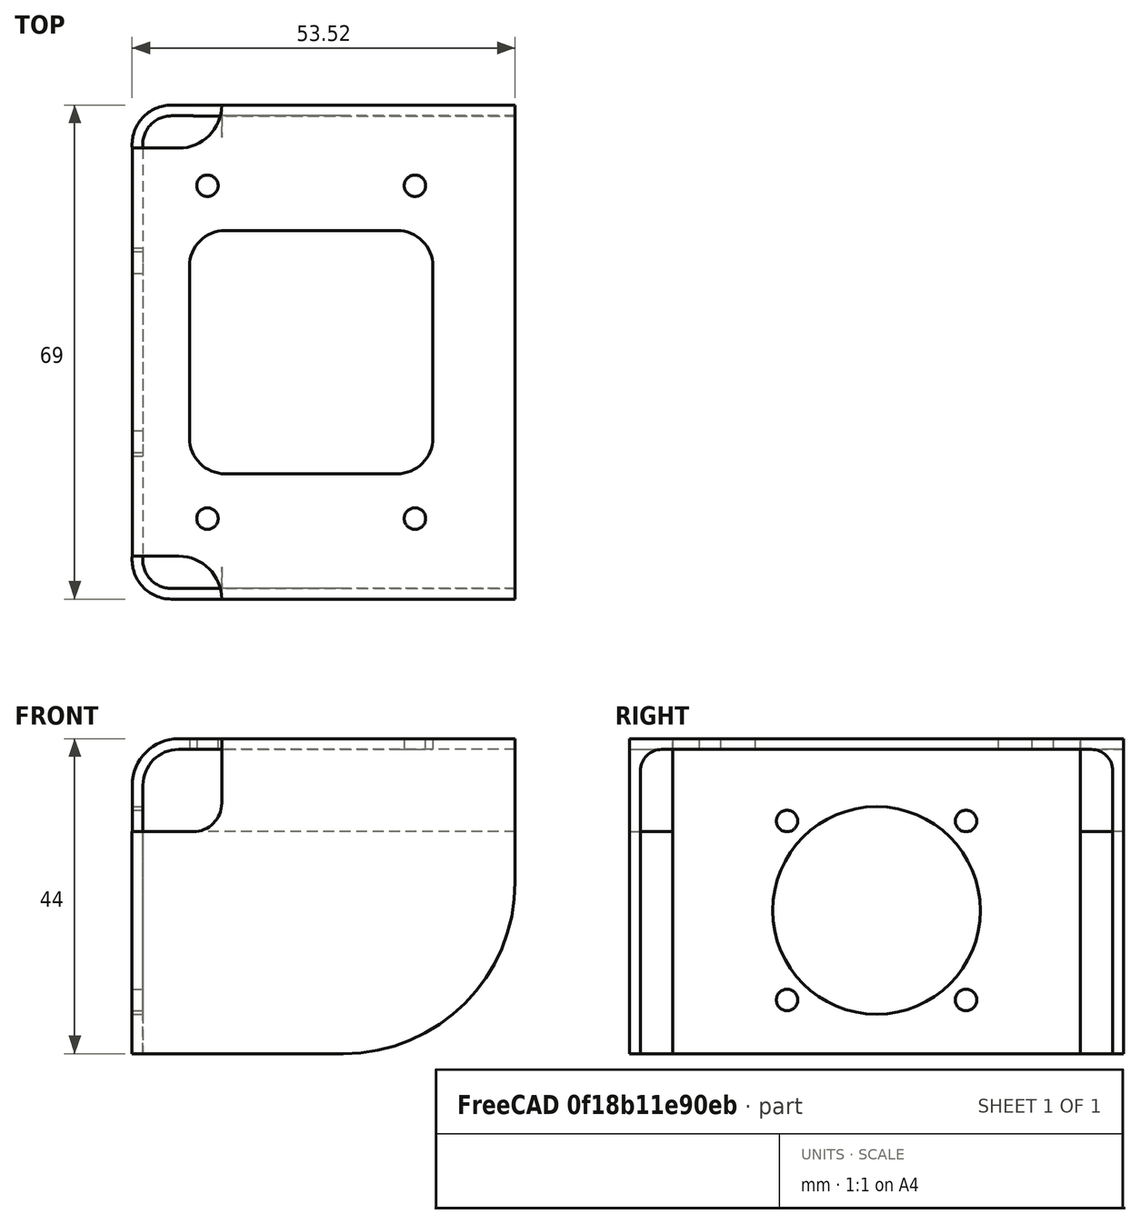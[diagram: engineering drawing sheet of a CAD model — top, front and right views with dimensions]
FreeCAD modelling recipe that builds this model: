
FCSTD DOCUMENT  (FreeCAD 0.19R)
Label: tole_adaptation_extrudeur_tete_mobile
License: All rights reserved
LicenseURL: http://en.wikipedia.org/wiki/All_rights_reserved
objects: TechDraw::DrawViewDimension×19, Sketcher::SketchObject×5, TechDraw::DrawViewPart×4, PartDesign::Pad×3, PartDesign::Pocket×2, PartDesign::Fillet×2, PartDesign::Mirrored×1, PartDesign::Body×1, TechDraw::DrawSVGTemplate×1, TechDraw::DrawPage×1
note: 21 computed .brp shape members not serialized (recipe doc carries the construction recipe); baked Part::Feature solids carry a one-line shape summary decoded from their .brp

FEATURE [Sketcher::SketchObject] Sketch
  FullyConstrained = true
  MapMode = 5
  Placement = pos=(0,0,0) rot=(1,0,0;1.5708rad)
  Support = -> [XZ_Plane]
  sketch-geometry (8):
    g0: LineSegment StartX=0 StartY=-44 StartZ=0 EndX=0 EndY=-6.5 EndZ=0
    g1: LineSegment StartX=6.5 StartY=0 StartZ=0 EndX=53.5 EndY=0 EndZ=0
    g2: LineSegment StartX=53.5 StartY=0 StartZ=0 EndX=53.5 EndY=-1.5 EndZ=0
    g3: LineSegment StartX=53.5 StartY=-1.5 StartZ=0 EndX=6.5 EndY=-1.5 EndZ=0
    g4: LineSegment StartX=1.5 StartY=-6.5 StartZ=0 EndX=1.5 EndY=-44 EndZ=0
    g5: LineSegment StartX=1.5 StartY=-44 StartZ=0 EndX=0 EndY=-44 EndZ=0
    g6: ArcOfCircle CenterX=6.5 CenterY=-6.5 CenterZ=0 NormalX=0 NormalY=0 NormalZ=1 AngleXU=0 Radius=5 StartAngle=1.5708 EndAngle=3.14159
    g7: ArcOfCircle CenterX=6.5 CenterY=-6.5 CenterZ=0 NormalX=0 NormalY=0 NormalZ=1 AngleXU=0 Radius=6.5 StartAngle=1.5708 EndAngle=3.14159
  constraints (21):
    c: PointOnObject(g0,g-2)
    c: PointOnObject(g1,g-1)
    c: Coincident(g1,g2)
    c: Vertical(g2)
    c: Coincident(g2,g3)
    c: Horizontal(g3)
    c: Vertical(g4)
    c: Coincident(g4,g5)
    c: Coincident(g5,g0)
    c: Tangent(g4,g6) = -1.5708
    c: Tangent(g3,g6) = -1.5708
    c: Tangent(g0,g7) = 1.5708
    c: Tangent(g1,g7) = 1.5708
    c: Coincident(g7,g6)
    c: Vertical(g0)
    c: Horizontal(g1)
    c: Horizontal(g5)
    c: DistanceY(g2,g2) = 1.5
    c: Radius(g6) = 5
    c: DistanceX(g-1,g1) = 53.5
    c: DistanceY(g0,g-1) = 44
FEATURE [PartDesign::Pad] Pad
  Direction = (1,1,1)
  Length = 69
  Length2 = 100
  Midplane = true
  Placement = pos=(0,0,0) rot=(1,0,0;1.5708rad)
  Profile = -> Sketch
  Type = 0
FEATURE [Sketcher::SketchObject] Sketch001
  ExternalGeometry = -> [Pad]
  FullyConstrained = false
  MapMode = 5
  Placement = pos=(0,0,0) rot=(0,0,1;3.14159rad)
  Support = -> [Pad]
  sketch-geometry (21):
    g0: LineSegment StartX=-37 StartY=17 StartZ=0 EndX=-13 EndY=17 EndZ=0
    g1: LineSegment StartX=-8 StartY=12 StartZ=0 EndX=-8 EndY=-12 EndZ=0
    g2: LineSegment StartX=-13 StartY=-17 StartZ=0 EndX=-37 EndY=-17 EndZ=0
    g3: LineSegment StartX=-42 StartY=-12 StartZ=0 EndX=-42 EndY=12 EndZ=0
    g4: ArcOfCircle CenterX=-13 CenterY=12 CenterZ=0 NormalX=0 NormalY=0 NormalZ=1 AngleXU=0 Radius=5 StartAngle=0 EndAngle=1.5708
    g5: ArcOfCircle CenterX=-37 CenterY=12 CenterZ=0 NormalX=0 NormalY=0 NormalZ=1 AngleXU=0 Radius=5 StartAngle=1.5708 EndAngle=3.14159
    g6: ArcOfCircle CenterX=-37 CenterY=-12 CenterZ=0 NormalX=0 NormalY=0 NormalZ=1 AngleXU=0 Radius=5 StartAngle=3.14159 EndAngle=4.71239
    g7: ArcOfCircle CenterX=-13 CenterY=-12 CenterZ=0 NormalX=0 NormalY=0 NormalZ=1 AngleXU=0 Radius=5 StartAngle=4.71239 EndAngle=6.28319
    g8: LineSegment StartX=-25 StartY=36.475 StartZ=0 EndX=-25 EndY=-28.4606 EndZ=0
    g9: Circle CenterX=-39.5 CenterY=23.25 CenterZ=0 NormalX=0 NormalY=0 NormalZ=1 AngleXU=0 Radius=1.5
    g10: Circle CenterX=-10.5 CenterY=23.25 CenterZ=0 NormalX=0 NormalY=0 NormalZ=1 AngleXU=0 Radius=1.5
    g11: Circle CenterX=-10.5 CenterY=-23.25 CenterZ=0 NormalX=0 NormalY=0 NormalZ=1 AngleXU=0 Radius=1.5
    g12: Circle CenterX=-39.5 CenterY=-23.25 CenterZ=0 NormalX=0 NormalY=0 NormalZ=1 AngleXU=0 Radius=1.5
    g13: ArcOfCircle CenterX=-6.5 CenterY=34.5 CenterZ=0 NormalX=0 NormalY=0 NormalZ=1 AngleXU=0 Radius=6 StartAngle=3.14159 EndAngle=4.71239
    g14: LineSegment StartX=-6.5 StartY=28.5 StartZ=0 EndX=1 EndY=28.5 EndZ=0
    g15: LineSegment StartX=-12.5 StartY=34.5 StartZ=0 EndX=1 EndY=34.5 EndZ=0
    g16: LineSegment StartX=1 StartY=34.5 StartZ=0 EndX=1 EndY=28.5 EndZ=0
    g17: ArcOfCircle CenterX=-6.5 CenterY=-34.5 CenterZ=0 NormalX=0 NormalY=0 NormalZ=1 AngleXU=0 Radius=6 StartAngle=1.5708 EndAngle=3.14159
    g18: LineSegment StartX=-6.5 StartY=-28.5 StartZ=0 EndX=1 EndY=-28.5 EndZ=0
    g19: LineSegment StartX=1 StartY=-28.5 StartZ=0 EndX=1 EndY=-34.5 EndZ=0
    g20: LineSegment StartX=1 StartY=-34.5 StartZ=0 EndX=-12.5 EndY=-34.5 EndZ=0
  constraints (49):
    c: Horizontal(g0)
    c: Tangent(g0,g4) = 1.5708
    c: Tangent(g1,g4) = 1.5708
    c: Tangent(g3,g5) = 1.5708
    c: Tangent(g0,g5) = 1.5708
    c: Tangent(g2,g6) = 1.5708
    c: Tangent(g3,g6) = 1.5708
    c: Tangent(g2,g7) = 1.5708
    c: Tangent(g1,g7) = 1.5708
    c: Symmetric(g0,g0,g8)
    c: Symmetric(g3,g1,g8)
    c: Symmetric(g2,g2,g8)
    c: Symmetric(g3,g3,g-1)
    c: Radius(g4) = 5
    c: DistanceY(g2,g0) = 34
    c: DistanceX(g3,g1) = 34
    c: Equal(g4,g7)
    c: DistanceX(g1,g-1) = 8
    c: DistanceX(g9,g10) = 29
    c: Symmetric(g9,g10,g8)
    c: Symmetric(g9,g12,g-1)
    c: Symmetric(g12,g11,g8)
    c: Equal(g11,g12)
    c: Equal(g11,g10)
    c: Equal(g9,g10)
    c: Radius(g9) = 1.5
    c: DistanceY(g12,g9) = 46.5
    c: Coincident(g13,g-3)
    c: PointOnObject(g13,g-3)
    c: Horizontal(g14)
    c: Tangent(g14,g13) = -1.5708
    c: Coincident(g15,g13)
    c: Horizontal(g15)
    c: Coincident(g16,g15)
    c: Coincident(g16,g14)
    c: Vertical(g16)
    c: DistanceX(g-1,g15) = 1
    c: Radius(g13) = 6
    c: Coincident(g17,g-4)
    c: PointOnObject(g17,g-4)
    c: Tangent(g17,g18) = 1.5708
    c: Coincident(g18,g19)
    c: Vertical(g19)
    c: Coincident(g19,g20)
    c: Coincident(g20,g17)
    c: Horizontal(g20)
    c: DistanceX(g-1,g18) = 1
    c: Horizontal(g18)
    c: Equal(g17,g13)
FEATURE [PartDesign::Pocket] Pocket
  BaseFeature = -> Pad
  Length = 5
  Length2 = 100
  Placement = pos=(0,0,0) rot=(1,0,0;1.5708rad)
  Profile = -> Sketch001
  Type = 1
FEATURE [Sketcher::SketchObject] Sketch003
  FullyConstrained = true
  MapMode = 5
  Placement = pos=(0,0,0) rot=(0.57735,0.57735,0.57735;2.0944rad)
  Support = -> [YZ_Plane]
  sketch-geometry (10):
    g0: Circle CenterX=0 CenterY=-24 CenterZ=0 NormalX=0 NormalY=0 NormalZ=1 AngleXU=0 Radius=14.5
    g1: LineSegment StartX=-12.5 StartY=-11.5 StartZ=0 EndX=12.5 EndY=-11.5 EndZ=0
    g2: LineSegment StartX=12.5 StartY=-11.5 StartZ=0 EndX=12.5 EndY=-36.5 EndZ=0
    g3: LineSegment StartX=12.5 StartY=-36.5 StartZ=0 EndX=-12.5 EndY=-36.5 EndZ=0
    g4: LineSegment StartX=-12.5 StartY=-36.5 StartZ=0 EndX=-12.5 EndY=-11.5 EndZ=0
    g5: Circle CenterX=12.5 CenterY=-11.5 CenterZ=0 NormalX=0 NormalY=0 NormalZ=1 AngleXU=0 Radius=1.5
    g6: Circle CenterX=-12.5 CenterY=-11.5 CenterZ=0 NormalX=0 NormalY=0 NormalZ=1 AngleXU=0 Radius=1.5
    g7: Circle CenterX=-12.5 CenterY=-36.5 CenterZ=0 NormalX=0 NormalY=0 NormalZ=1 AngleXU=0 Radius=1.5
    g8: Circle CenterX=12.5 CenterY=-36.5 CenterZ=0 NormalX=0 NormalY=0 NormalZ=1 AngleXU=0 Radius=1.5
    g9: LineSegment StartX=-12.5 StartY=-11.5 StartZ=0 EndX=12.5 EndY=-36.5 EndZ=0
  constraints (24):
    c: Radius(g0) = 14.5
    c: Coincident(g1,g2)
    c: Coincident(g2,g3)
    c: Coincident(g3,g4)
    c: Coincident(g4,g1)
    c: Horizontal(g3)
    c: Vertical(g2)
    c: Coincident(g5,g1)
    c: Coincident(g6,g1)
    c: Coincident(g7,g3)
    c: Coincident(g8,g2)
    c: Equal(g8,g5)
    c: Equal(g5,g6)
    c: Equal(g6,g7)
    c: Radius(g6) = 1.5
    c: DistanceY(g2,g2) = 25
    c: DistanceX(g1,g1) = 25
    c: Coincident(g9,g6)
    c: Coincident(g9,g8)
    c: PointOnObject(g0,g9)
    c: Vertical(g4)
    c: Symmetric(g5,g6,g-2)
    c: PointOnObject(g0,g-2)
    c: DistanceY(g0,g-1) = 24
FEATURE [PartDesign::Pocket] Pocket001
  BaseFeature = -> Pocket
  Length = 5
  Length2 = 100
  Midplane = true
  Placement = pos=(0,0,0) rot=(1,0,0;1.5708rad)
  Profile = -> Sketch003
  Type = 1
FEATURE [Sketcher::SketchObject] Sketch004
  ExternalGeometry = -> [Pocket001]
  FullyConstrained = true
  MapMode = 5
  Placement = pos=(0,-6.84e-14,-44) rot=(1,0,0;3.14159rad)
  Support = -> [Pocket001]
  sketch-geometry (6):
    g0: ArcOfCircle CenterX=5.4675 CenterY=29.0089 CenterZ=0 NormalX=0 NormalY=0 NormalZ=1 AngleXU=0 Radius=4 StartAngle=1.5708 EndAngle=3.26916
    g1: ArcOfCircle CenterX=5.4675 CenterY=29.0089 CenterZ=0 NormalX=0 NormalY=0 NormalZ=1 AngleXU=0 Radius=5.49113 StartAngle=1.5708 EndAngle=3.2344
    g2: LineSegment StartX=5.4675 StartY=34.5 StartZ=0 EndX=53.5 EndY=34.5 EndZ=0
    g3: LineSegment StartX=53.5 StartY=34.5 StartZ=0 EndX=53.5 EndY=33.0089 EndZ=0
    g4: LineSegment StartX=53.5 StartY=33.0089 StartZ=0 EndX=5.4675 EndY=33.0089 EndZ=0
    g5: LineSegment StartX=0 StartY=28.5 StartZ=0 EndX=1.5 EndY=28.5 EndZ=0
  constraints (14):
    c: Coincident(g1,g0)
    c: Tangent(g1,g2) = 1.5708
    c: Coincident(g2,g3)
    c: Vertical(g3)
    c: Coincident(g3,g4)
    c: Horizontal(g4)
    c: Horizontal(g2)
    c: Radius(g0) = 4
    c: Coincident(g5,g1)
    c: Coincident(g5,g0)
    c: Coincident(g-3,g0)
    c: Coincident(g1,g-4)
    c: Tangent(g4,g0) = -1.5708
    c: Coincident(g-5,g2)
FEATURE [PartDesign::Pad] Pad001
  BaseFeature = -> Pocket001
  Direction = (1,1,1)
  Length = 31
  Length2 = 100
  Placement = pos=(0,0,0) rot=(1,0,0;1.5708rad)
  Profile = -> Sketch004
  Reversed = true
  Type = 0
FEATURE [Sketcher::SketchObject] Sketch005
  ExternalGeometry = -> [Pad001]
  FullyConstrained = true
  MapMode = 5
  Placement = pos=(0,-34.5,6.89e-14) rot=(1,0,0;1.5708rad)
  Support = -> [Pad001]
  sketch-geometry (5):
    g0: LineSegment StartX=53.5 StartY=-1.5 StartZ=0 EndX=12.5 EndY=-1.5 EndZ=0
    g1: LineSegment StartX=12.5 StartY=-1.5 StartZ=0 EndX=12.5 EndY=-9 EndZ=0
    g2: LineSegment StartX=8.5 StartY=-13 StartZ=0 EndX=53.5 EndY=-13 EndZ=0
    g3: LineSegment StartX=53.5 StartY=-13 StartZ=0 EndX=53.5 EndY=-1.5 EndZ=0
    g4: ArcOfCircle CenterX=8.5 CenterY=-9 CenterZ=0 NormalX=0 NormalY=0 NormalZ=1 AngleXU=0 Radius=4 StartAngle=4.71239 EndAngle=6.28319
  constraints (11):
    c: Coincident(g0,g1)
    c: Coincident(g2,g3)
    c: Coincident(g3,g0)
    c: Horizontal(g2)
    c: Vertical(g1)
    c: Coincident(g0,g-3)
    c: Coincident(g2,g-4)
    c: Coincident(g0,g-5)
    c: Tangent(g4,g1) = 1.5708
    c: Tangent(g4,g2) = -1.5708
    c: Radius(g4) = 4
FEATURE [PartDesign::Pad] Pad002
  BaseFeature = -> Pad001
  Direction = (1,1,1)
  Length = 1.5
  Length2 = 100
  Placement = pos=(0,0,0) rot=(1,0,0;1.5708rad)
  Profile = -> Sketch005
  Reversed = true
  Type = 0
FEATURE [PartDesign::Fillet] Fillet
  Base = -> Pad002 [Edge60]
  BaseFeature = -> Pad002
  Placement = pos=(0,0,0) rot=(1,0,0;1.5708rad)
  Radius = 3
  SupportTransform = false
FEATURE [PartDesign::Mirrored] Mirrored
  BaseFeature = -> Fillet
  MirrorPlane = -> XZ_Plane
  Originals = -> [Pad001,Pad002,Fillet]
  Placement = pos=(0,0,0) rot=(1,0,0;1.5708rad)
FEATURE [PartDesign::Fillet] Fillet001
  Base = -> Mirrored [Edge64,Edge105]
  BaseFeature = -> Mirrored
  Placement = pos=(0,0,0) rot=(1,0,0;1.5708rad)
  Radius = 24
  SupportTransform = false
FEATURE [PartDesign::Body] Body
  Group = -> [Sketch,Pad,Sketch001,Pocket,Sketch003,Pocket001,Sketch004,Pad001,Sketch005,Pad002,Fillet,Mirrored,Fillet001]
  Origin = -> Origin
  Tip = -> Fillet001
FEATURE [TechDraw::DrawSVGTemplate] Template
  EditableTexts = Designed_by_Name=JC Carré; Drawing_number=1/2; FC-Date=23/06/2021; FC-SC=3:2; FC-SH=1/2; FC-Title=équerre adaptation etrudeur
  Height = 210
  Orientation = 1
  Width = 297
FEATURE [TechDraw::DrawViewPart] View
  CoarseView = false
  Direction = (0,-1,0)
  Focus = 100
  HardHidden = false
  IsoCount = 0
  IsoHidden = false
  IsoVisible = false
  LockPosition = false
  Perspective = false
  Rotation = 0
  Scale = 1.5
  ScaleType = 0
  SeamHidden = false
  SeamVisible = true
  SmoothHidden = false
  SmoothVisible = true
  Source = -> [Body]
  X = 177.794
  XDirection = (1,0,0)
  Y = 159.179
FEATURE [TechDraw::DrawViewPart] View001
  CoarseView = false
  Direction = (1,0,0)
  Focus = 100
  HardHidden = false
  IsoCount = 0
  IsoHidden = false
  IsoVisible = false
  LockPosition = false
  Perspective = false
  Rotation = 0
  Scale = 1.5
  ScaleType = 0
  SeamHidden = false
  SeamVisible = true
  SmoothHidden = false
  SmoothVisible = true
  Source = -> [Body]
  X = 73.3588
  XDirection = (0,1,0)
  Y = 158.489
FEATURE [TechDraw::DrawViewDimension] Dimension004
  Arbitrary = false
  ArbitraryTolerances = false
  EqualTolerance = true
  FormatSpec = ⌀%.0f
  FormatSpecTolerance = %+.0f
  Inverted = false
  LockPosition = false
  MeasureType = 1
  OverTolerance = 0
  References2D = -> [View001]
  Rotation = 0
  Scale = 1.5
  ScaleType = 0
  TheoreticalExact = false
  Type = 5
  UnderTolerance = 0
  X = 26.0913
  Y = -22.8042
FEATURE [TechDraw::DrawViewDimension] Dimension006
  Arbitrary = false
  ArbitraryTolerances = false
  EqualTolerance = true
  FormatSpec = %.0f
  FormatSpecTolerance = %+.0f
  Inverted = false
  LockPosition = false
  MeasureType = 1
  OverTolerance = 0
  References2D = -> [View001]
  Rotation = 0
  Scale = 1.5
  ScaleType = 0
  TheoreticalExact = false
  Type = 1
  UnderTolerance = 0
  X = -1.42669
  Y = 29.6176
FEATURE [TechDraw::DrawViewDimension] Dimension007
  Arbitrary = false
  ArbitraryTolerances = false
  EqualTolerance = true
  FormatSpec = %.0f
  FormatSpecTolerance = %+.0f
  Inverted = false
  LockPosition = false
  MeasureType = 1
  OverTolerance = 0
  References2D = -> [View001]
  Rotation = 0
  Scale = 1.5
  ScaleType = 0
  TheoreticalExact = false
  Type = 2
  UnderTolerance = 0
  X = 25.7967
  Y = -1.85733
FEATURE [TechDraw::DrawViewPart] View002
  CoarseView = false
  Direction = (0,0,1)
  Focus = 100
  HardHidden = false
  IsoCount = 0
  IsoHidden = false
  IsoVisible = false
  LockPosition = false
  Perspective = false
  Rotation = 0
  Scale = 1.5
  ScaleType = 0
  SeamHidden = false
  SeamVisible = true
  SmoothHidden = false
  SmoothVisible = true
  Source = -> [Body]
  X = 73.7147
  XDirection = (0,1,0)
  Y = 60.2081
FEATURE [TechDraw::DrawViewDimension] Dimension008
  Arbitrary = false
  ArbitraryTolerances = false
  EqualTolerance = true
  FormatSpec = %.0f
  FormatSpecTolerance = %+.0f
  Inverted = false
  LockPosition = false
  MeasureType = 1
  OverTolerance = 0
  References2D = -> [View002]
  Rotation = 0
  Scale = 1.5
  ScaleType = 0
  TheoreticalExact = false
  Type = 2
  UnderTolerance = 0
  X = -18
  Y = 2.60728
FEATURE [TechDraw::DrawViewDimension] Dimension009
  Arbitrary = false
  ArbitraryTolerances = false
  EqualTolerance = true
  FormatSpec = %.0f
  FormatSpecTolerance = %+.0f
  Inverted = false
  LockPosition = false
  MeasureType = 1
  OverTolerance = 0
  References2D = -> [View002]
  Rotation = 0
  Scale = 1.5
  ScaleType = 0
  TheoreticalExact = false
  Type = 1
  UnderTolerance = 0
  X = 4.09e-14
  Y = 20.6073
FEATURE [TechDraw::DrawViewDimension] Dimension010
  Arbitrary = false
  ArbitraryTolerances = false
  EqualTolerance = true
  FormatSpec = ⌀%.0f
  FormatSpecTolerance = %+.0f
  Inverted = false
  LockPosition = false
  MeasureType = 1
  OverTolerance = 0
  References2D = -> [View002]
  Rotation = 0
  Scale = 1.5
  ScaleType = 0
  TheoreticalExact = false
  Type = 5
  UnderTolerance = 0
  X = -47.6359
  Y = 16.6913
FEATURE [TechDraw::DrawViewDimension] Dimension011
  Arbitrary = false
  ArbitraryTolerances = false
  EqualTolerance = true
  FormatSpec = %.0f
  FormatSpecTolerance = %+.0f
  Inverted = false
  LockPosition = false
  MeasureType = 1
  OverTolerance = 0
  References2D = -> [View002]
  Rotation = 0
  Scale = 1.5
  ScaleType = 0
  TheoreticalExact = false
  Type = 1
  UnderTolerance = 0
  X = -2.73924
  Y = -25.9908
FEATURE [TechDraw::DrawViewDimension] Dimension012
  Arbitrary = false
  ArbitraryTolerances = false
  EqualTolerance = true
  FormatSpec = %.0f
  FormatSpecTolerance = %+.0f
  Inverted = false
  LockPosition = false
  MeasureType = 1
  OverTolerance = 0
  References2D = -> [View002]
  Rotation = 0
  Scale = 1.5
  ScaleType = 0
  TheoreticalExact = false
  Type = 2
  UnderTolerance = 0
  X = 31.7838
  Y = 2.72617
FEATURE [TechDraw::DrawViewDimension] Dimension013
  Arbitrary = false
  ArbitraryTolerances = false
  EqualTolerance = true
  FormatSpec = %.0f
  FormatSpecTolerance = %+.0f
  Inverted = false
  LockPosition = false
  MeasureType = 1
  OverTolerance = 0
  References2D = -> [View002]
  Rotation = 0
  Scale = 1.5
  ScaleType = 0
  TheoreticalExact = false
  Type = 2
  UnderTolerance = 0
  X = 51.8717
  Y = -1.00385
FEATURE [TechDraw::DrawViewDimension] Dimension
  Arbitrary = false
  ArbitraryTolerances = false
  EqualTolerance = true
  FormatSpec = %.0f
  FormatSpecTolerance = %+.0f
  Inverted = false
  LockPosition = false
  MeasureType = 1
  OverTolerance = 0
  References2D = -> [View]
  Rotation = 0
  Scale = 1.5
  ScaleType = 0
  TheoreticalExact = false
  Type = 2
  UnderTolerance = 0
  X = 40.4975
  Y = 0.340652
FEATURE [TechDraw::DrawViewDimension] Dimension014
  Arbitrary = false
  ArbitraryTolerances = false
  EqualTolerance = true
  FormatSpec = %.0f
  FormatSpecTolerance = %+.0f
  Inverted = false
  LockPosition = false
  MeasureType = 1
  OverTolerance = 0
  References2D = -> [View]
  Rotation = 0
  Scale = 1.5
  ScaleType = 0
  TheoreticalExact = false
  Type = 1
  UnderTolerance = 0
  X = -5.14035
  Y = -35.8027
FEATURE [TechDraw::DrawViewDimension] Dimension015
  Arbitrary = false
  ArbitraryTolerances = false
  EqualTolerance = true
  FormatSpec = %.0f
  FormatSpecTolerance = %+.0f
  Inverted = false
  LockPosition = false
  MeasureType = 1
  OverTolerance = 0
  References2D = -> [View002]
  Rotation = 0
  Scale = 1.5
  ScaleType = 0
  TheoreticalExact = false
  Type = 2
  UnderTolerance = 0
  X = -62.5126
  Y = 33.5186
FEATURE [TechDraw::DrawViewDimension] Dimension016
  Arbitrary = false
  ArbitraryTolerances = false
  EqualTolerance = true
  FormatSpec = %.0f
  FormatSpecTolerance = %+.0f
  Inverted = false
  LockPosition = false
  MeasureType = 1
  OverTolerance = 0
  References2D = -> [View002]
  Rotation = 0
  Scale = 1.5
  ScaleType = 0
  TheoreticalExact = false
  Type = 2
  UnderTolerance = 0
  X = 61.9173
  Y = 36.3672
FEATURE [TechDraw::DrawViewDimension] Dimension017
  Arbitrary = false
  ArbitraryTolerances = false
  EqualTolerance = true
  FormatSpec = %.0f
  FormatSpecTolerance = %+.0f
  Inverted = false
  LockPosition = false
  MeasureType = 1
  OverTolerance = 0
  References2D = -> [View001]
  Rotation = 0
  Scale = 1.5
  ScaleType = 0
  TheoreticalExact = false
  Type = 2
  UnderTolerance = 0
  X = -35.8018
  Y = -24.7042
FEATURE [TechDraw::DrawViewDimension] Dimension018
  Arbitrary = false
  ArbitraryTolerances = false
  EqualTolerance = true
  FormatSpec = %.0f
  FormatSpecTolerance = %+.0f
  Inverted = false
  LockPosition = false
  MeasureType = 1
  OverTolerance = 0
  References2D = -> [View001]
  Rotation = 0
  Scale = 1.5
  ScaleType = 0
  TheoreticalExact = false
  Type = 2
  UnderTolerance = 0
  X = -10.0667
  Y = -11.4258
FEATURE [TechDraw::DrawViewDimension] Dimension019
  Arbitrary = false
  ArbitraryTolerances = false
  EqualTolerance = true
  FormatSpec = %.0f
  FormatSpecTolerance = %+.0f
  Inverted = false
  LockPosition = false
  MeasureType = 1
  OverTolerance = 0
  References2D = -> [View001]
  Rotation = 0
  Scale = 1.5
  ScaleType = 0
  TheoreticalExact = false
  Type = 2
  UnderTolerance = 0
  X = -63.532
  Y = -0.185835
FEATURE [TechDraw::DrawViewDimension] Dimension020
  Arbitrary = false
  ArbitraryTolerances = false
  EqualTolerance = true
  FormatSpec = ⌀%.0f
  FormatSpecTolerance = %+.0f
  Inverted = false
  LockPosition = false
  MeasureType = 1
  OverTolerance = 0
  References2D = -> [View001]
  Rotation = 0
  Scale = 1.5
  ScaleType = 0
  TheoreticalExact = false
  Type = 5
  UnderTolerance = 0
  X = 4.10886
  Y = -1.84899
FEATURE [TechDraw::DrawViewPart] View003
  CoarseView = false
  Direction = (0.84,0.391,-0.376)
  Focus = 100
  HardHidden = false
  IsoCount = 0
  IsoHidden = false
  IsoVisible = false
  LockPosition = false
  Perspective = false
  Rotation = 0
  Scale = 0.75
  ScaleType = 0
  SeamHidden = false
  SeamVisible = true
  SmoothHidden = false
  SmoothVisible = true
  Source = -> [Body]
  X = 248.735
  XDirection = (-0.419,0.908,0.008)
  Y = 89.1485
FEATURE [TechDraw::DrawViewDimension] Dimension021
  Arbitrary = false
  ArbitraryTolerances = false
  EqualTolerance = true
  FormatSpec = %.0f
  FormatSpecTolerance = %+.0f
  Inverted = false
  LockPosition = false
  MeasureType = 1
  OverTolerance = 0
  References2D = -> [View002]
  Rotation = 0
  Scale = 1.5
  ScaleType = 0
  TheoreticalExact = false
  Type = 1
  UnderTolerance = 0
  X = 1.18335
  Y = 51.2369
FEATURE [TechDraw::DrawViewDimension] Dimension022
  Arbitrary = false
  ArbitraryTolerances = false
  EqualTolerance = true
  FormatSpec = %.0f
  FormatSpecTolerance = %+.0f
  Inverted = false
  LockPosition = false
  MeasureType = 1
  OverTolerance = 0
  References2D = -> [View001]
  Rotation = 0
  Scale = 1.5
  ScaleType = 0
  TheoreticalExact = false
  Type = 1
  UnderTolerance = 0
  X = -8.81444
  Y = 41.7605
FEATURE [TechDraw::DrawPage] Page
  KeepUpdated = true
  NextBalloonIndex = 1
  ProjectionType = 0
  Scale = 1.5
  Template = -> Template
  Views = -> [View,View001,Dimension004,Dimension006,Dimension007,View002,Dimension008,Dimension009,Dimension010,Dimension011,Dimension012,Dimension013,Dimension,Dimension014,Dimension015,Dimension016,Dimension017,Dimension018,Dimension019,Dimension020,View003,Dimension021,Dimension022]
